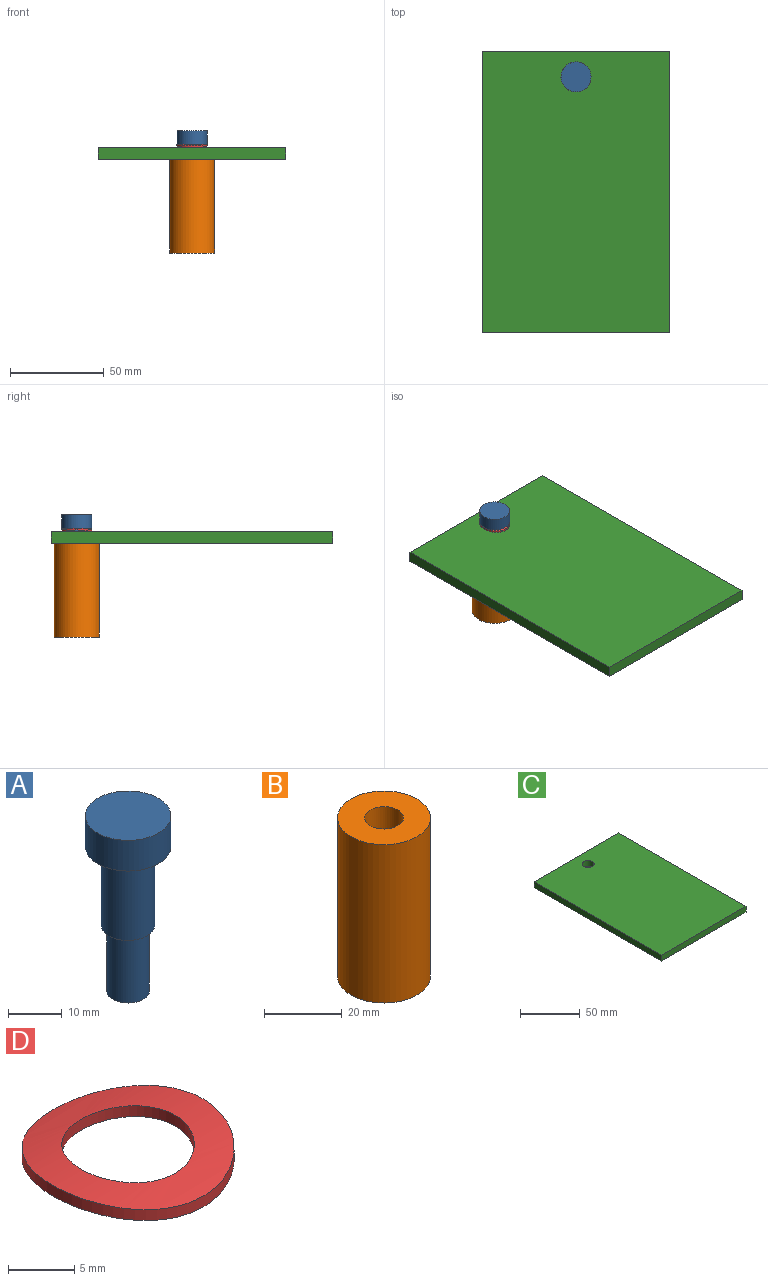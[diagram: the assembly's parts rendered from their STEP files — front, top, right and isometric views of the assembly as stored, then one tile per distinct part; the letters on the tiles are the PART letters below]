
ASSEMBLY  parts=4 mates=3
PART A: 7 faces, bbox 16x16x40 mm
  f0: cylinder r=5mm len=18mm, axis (0,0,1), area 565.5mm2, adj f1,f6
  f1: plane 10x10mm, normal (0,0,-1), area 28.3mm2, adj f0,f2
  f2: cylinder r=4mm len=15mm, axis (0,0,1), area 377mm2, adj f1,f3
  f3: plane 8x8mm, normal (0,0,-1), area 50.3mm2, adj f2
  f4: cylinder r=8mm len=16mm, axis (0,0,-1), area 351.9mm2, adj f5,f6
  f5: plane 16x16mm, normal (0,0,1), area 201.1mm2, adj f4
  f6: plane 16x16mm, normal (0,0,-1), area 122.5mm2, adj f0,f4
PART B: 7 faces, bbox 24x24x50 mm
  f0: cylinder r=12mm len=50mm, axis (0,0,1), area 3769.9mm2, adj f1,f2
  f1: plane 24x24mm, normal (0,0,-1), area 452.4mm2, adj f0
  f2: plane 24x24mm, normal (0,0,1), area 373.8mm2, adj f0,f3
  f3: cylinder r=5mm len=10mm, axis (0,0,1), area 314.2mm2, adj f2,f4
  f4: plane 10x10mm, normal (0,0,1), area 28.3mm2, adj f3,f5
  f5: cylinder r=4mm len=15mm, axis (0,0,1), area 377mm2, adj f4,f6
  f6: plane 8x8mm, normal (0,0,1), area 50.3mm2, adj f5
PART C: 7 faces, bbox 100x150x6 mm
  f0: plane 150x100mm, normal (0,0,1), area 14921.5mm2, adj f1,f3,f4,f5,f6
  f1: plane 150x6mm, normal (-1,0,0), area 900mm2, adj f0,f2,f4,f5
  f2: plane 150x100mm, normal (0,0,-1), area 14921.5mm2, adj f1,f3,f4,f5,f6
  f3: plane 150x6mm, normal (1,0,0), area 900mm2, adj f0,f2,f4,f5
  f4: plane 100x6mm, normal (0,-1,0), area 600mm2, adj f0,f1,f2,f3
  f5: plane 100x6mm, normal (0,1,0), area 600mm2, adj f0,f1,f2,f3
  f6: cylinder r=5mm len=10mm, axis (0,0,1), area 188.5mm2, adj f0,f2
PART D: 4 faces, bbox 16x16x2 mm
  f0: cylinder r=32.5mm len=16mm, axis (-1,0,0), area 123.8mm2, adj f2,f3
  f1: cylinder r=32.5mm len=16mm, axis (-1,0,0), area 123.8mm2, adj f2,f3
  f2: cylinder r=5mm len=10mm, axis (0,0,1), area 31.4mm2, adj f0,f1
  f3: cylinder r=8mm len=16mm, axis (0,0,1), area 50.3mm2, adj f0,f1
PLACE A t=(-52.63,-30.34,26.29)mm
PLACE B t=(-58.38,3.09,18.29)mm
PLACE C t=(-49.9,37.18,4.68)mm
PLACE D t=(-95.12,-3.36,-12.84)mm
MATE fastened B.f0 <-> A.f0  axis (0,0,1) through (-87.12,23.44,8.29)mm
MATE fastened D.f2 <-> A.f0  axis (0,0,1) through (-87.12,23.44,26.29)mm
MATE fastened B.f0 <-> C.f6  axis (0,0,1) through (-87.12,23.44,18.29)mm
